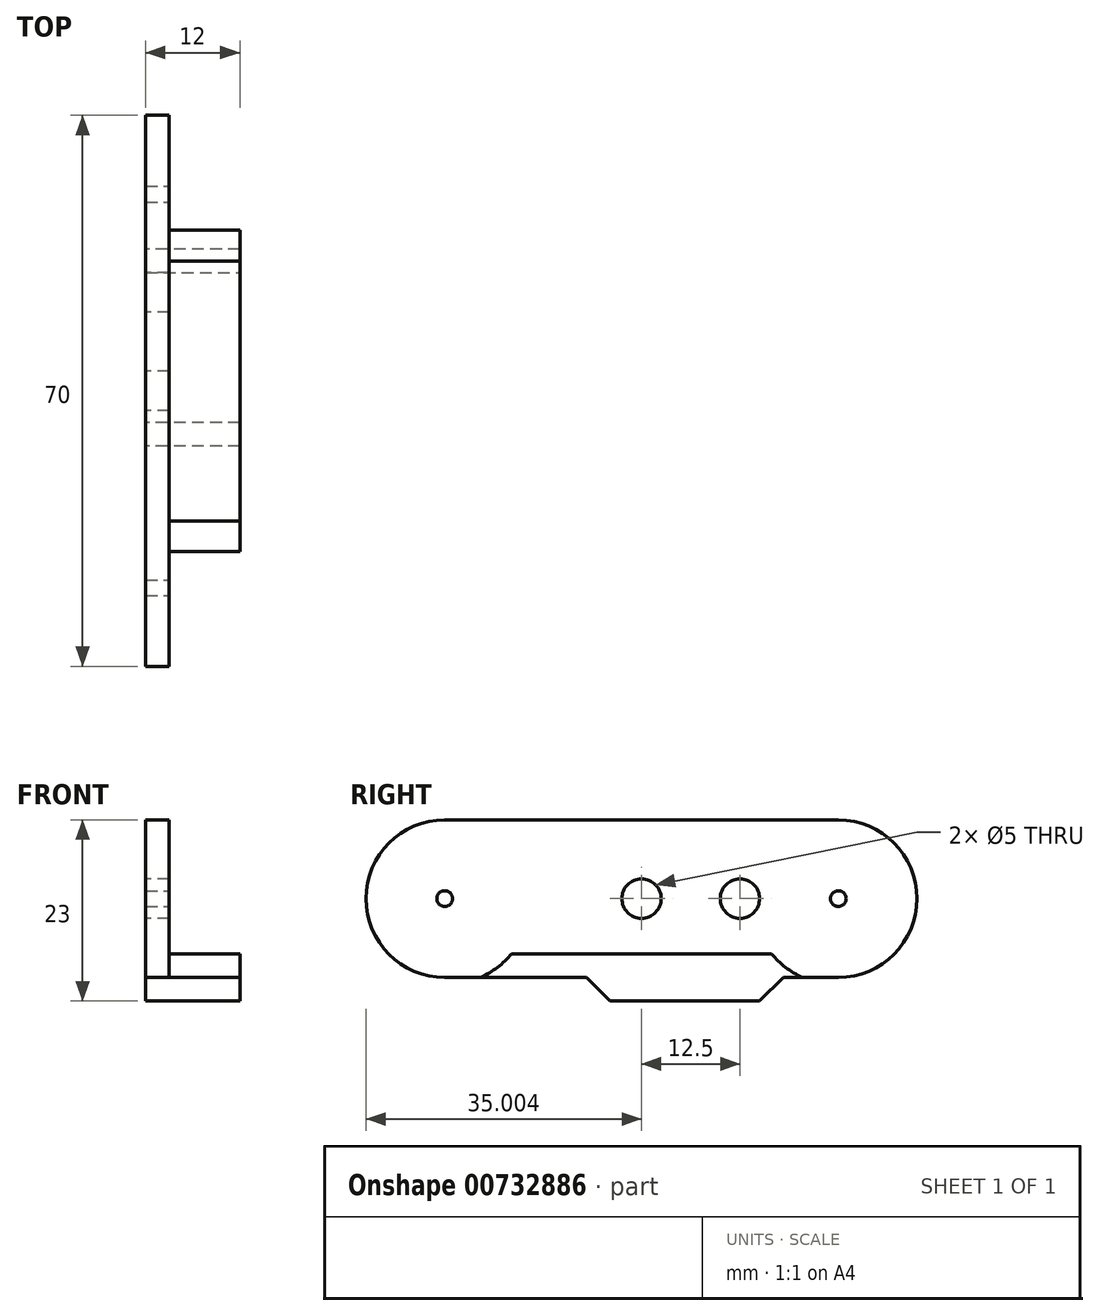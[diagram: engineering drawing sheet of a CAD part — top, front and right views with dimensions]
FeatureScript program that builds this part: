
annotation { "Feature Type Name" : "Feature", "Feature Type Description" : "" }
export const myFeature = defineFeature(function(context is Context, id is Id, definition is map)
    precondition{}
    {
        {
            var Q0;
            Q0=qCreatedBy(makeId("Right.planeOp"),FACE);
            var sketch = newSketch(context, id + "F0", { "sketchPlane" : qUnion([Q0])});
            skLineSegment(sketch, "E0.bottom", {"start": v(50.2, 39.59) * mm, "end": v(-19.8, 39.59) * mm});
            skLineSegment(sketch, "E0.top", {"start": v(50.2, 19.59) * mm, "end": v(-19.8, 19.59) * mm});
            skLineSegment(sketch, "E0.left", {"start": v(50.2, 39.59) * mm, "end": v(50.2, 19.59) * mm});
            skLineSegment(sketch, "E0.right", {"start": v(-19.8, 39.59) * mm, "end": v(-19.8, 19.59) * mm});
            skSolve(sketch);
        }
        {
            var Q0;
            Q0=makeQuery(id+"F0.imprint","IMPRINT",FACE,{"disambiguationData":[TD([[makeQuery(id+"F0.imprint","IMPRINT",EDGE,{"derivedFrom":sQuery(id+"F0.wireOp",EDGE,"E0.bottom")}),1.0]])]});
            extrude(context, id + "F1", {"entities" : qUnion([Q0]), "depth" : 3 * mm, "offsetDistance" : 25 * mm});
        }
        {
            var Q0;
            Q0=makeQuery(id+"F1.opExtrude","CAP_FACE",FACE,{"disambiguationData":[OSD([sQuery(id+"F0.wireOp",EDGE,"E0.bottom"),sQuery(id+"F0.wireOp",EDGE,"E0.top"),sQuery(id+"F0.wireOp",EDGE,"E0.left"),sQuery(id+"F0.wireOp",EDGE,"E0.right")])],"isStart":false});
            var sketch = newSketch(context, id + "F2", { "sketchPlane" : qUnion([Q0])});
            skLineSegment(sketch, "E1.bottom", {"start": v(-19.8, 19.59) * mm, "end": v(50.2, 19.59) * mm});
            skLineSegment(sketch, "E1.top", {"start": v(-19.8, 22.59) * mm, "end": v(50.2, 22.59) * mm});
            skLineSegment(sketch, "E1.left", {"start": v(-19.8, 19.59) * mm, "end": v(-19.8, 22.59) * mm});
            skLineSegment(sketch, "E1.right", {"start": v(50.2, 19.59) * mm, "end": v(50.2, 22.59) * mm});
            skLineSegment(sketch, "E2.bottom", {"start": v(-19.8, 39.59) * mm, "end": v(0.2, 39.59) * mm});
            skLineSegment(sketch, "E2.top", {"start": v(-19.8, 19.59) * mm, "end": v(0.2, 19.59) * mm});
            skLineSegment(sketch, "E2.left", {"start": v(-19.8, 39.59) * mm, "end": v(-19.8, 19.59) * mm});
            skLineSegment(sketch, "E2.right", {"start": v(0.2, 39.59) * mm, "end": v(0.2, 19.59) * mm});
            skLineSegment(sketch, "E3.bottom", {"start": v(50.2, 39.59) * mm, "end": v(40.2, 39.59) * mm});
            skLineSegment(sketch, "E3.top", {"start": v(50.2, 19.59) * mm, "end": v(40.2, 19.59) * mm});
            skLineSegment(sketch, "E3.left", {"start": v(50.2, 39.59) * mm, "end": v(50.2, 19.59) * mm});
            skLineSegment(sketch, "E3.right", {"start": v(40.2, 39.59) * mm, "end": v(40.2, 19.59) * mm});
            skCircle(sketch, "E4", {"center": v(40.2, 29.59) * mm, "radius": 11 * mm});
            skCircle(sketch, "E5", {"center": v(-9.8, 29.59) * mm, "radius": 11 * mm});
            skPoint(sketch, "E5.centerSnap0", {"position": v(-19.8, 29.59) * mm});
            skPoint(sketch, "E5.centerSnap1", {"position": v(-9.8, 39.59) * mm});
            skSolve(sketch);
        }
        {
            var Q0;
            {var subQ0=sQuery(id+"F2.wireOp",EDGE,"E5");var subQ1=sQuery(id+"F2.wireOp",EDGE,"E1.top");var subQ2=makeQuery(id+"F2.imprint","INTERSECT",VERTEX,{"disambiguationData":[OD(1.0)],"derivedFrom":[subQ1,subQ0]});Q0=makeQuery(id+"F2.imprint","IMPRINT",FACE,{"disambiguationData":[TD([[makeQuery(id+"F2.imprint","IMPRINT",EDGE,{"disambiguationData":[TD([[subQ2,-1.0]])],"derivedFrom":subQ1}),-1.0]])]});}
            var Q1;
            {var subQ0=sQuery(id+"F2.wireOp",EDGE,"E2.right");var subQ5=sQuery(id+"F2.wireOp",EDGE,"E1.top");var subQ7=makeQuery(id+"F2.imprint","INTERSECT",VERTEX,{"derivedFrom":[subQ5,subQ0]});Q1=makeQuery(id+"F2.imprint","IMPRINT",FACE,{"disambiguationData":[TD([[makeQuery(id+"F2.imprint","IMPRINT",EDGE,{"disambiguationData":[TD([[subQ7,-1.0]])],"derivedFrom":subQ5}),-1.0]])]});}
            extrude(context, id + "F3", {"entities" : qUnion([Q0, Q1]), "operationType" : NewBodyOperationType.ADD, "depth" : 9 * mm, "offsetDistance" : 25 * mm});
        }
        {
            var Q0;
            Q0=makeQuery(id+"F1.opExtrude","CAP_FACE",FACE,{"disambiguationData":[OSD([sQuery(id+"F0.wireOp",EDGE,"E0.bottom"),sQuery(id+"F0.wireOp",EDGE,"E0.top"),sQuery(id+"F0.wireOp",EDGE,"E0.left"),sQuery(id+"F0.wireOp",EDGE,"E0.right")])],"isStart":true});
            var sketch = newSketch(context, id + "F4", { "sketchPlane" : qUnion([Q0])});
            skLineSegment(sketch, "E6.bottom", {"start": v(19.8, 39.59) * mm, "end": v(-0.2, 39.59) * mm});
            skLineSegment(sketch, "E6.top", {"start": v(19.8, 19.59) * mm, "end": v(-0.2, 19.59) * mm});
            skLineSegment(sketch, "E6.left", {"start": v(19.8, 39.59) * mm, "end": v(19.8, 19.59) * mm});
            skLineSegment(sketch, "E6.right", {"start": v(-0.2, 39.59) * mm, "end": v(-0.2, 19.59) * mm});
            skCircle(sketch, "E7", {"center": v(9.8, 29.59) * mm, "radius": 10 * mm});
            skLineSegment(sketch, "E8.bottom", {"start": v(9.8, 29.59) * mm, "end": v(-20.2, 29.59) * mm});
            skLineSegment(sketch, "E8.top", {"start": v(9.8, -0.41) * mm, "end": v(-20.2, -0.41) * mm});
            skLineSegment(sketch, "E8.left", {"start": v(9.8, 29.59) * mm, "end": v(9.8, -0.41) * mm});
            skLineSegment(sketch, "E8.right", {"start": v(-20.2, 29.59) * mm, "end": v(-20.2, -0.41) * mm});
            skLineSegment(sketch, "E9", {"start": v(9.8, 29.59) * mm, "end": v(-20.2, -0.41) * mm});
            skLineSegment(sketch, "E10", {"start": v(9.8, 29.59) * mm, "end": v(-4.35, 15.45) * mm});
            skCircle(sketch, "E11", {"center": v(-4.35, 15.45) * mm, "radius": 10 * mm});
            skCircle(sketch, "E12", {"center": v(-20.2, -0.41) * mm, "radius": 10 * mm});
            skLineSegment(sketch, "E13.bottom", {"start": v(-14.35, 25.45) * mm, "end": v(5.65, 25.45) * mm});
            skLineSegment(sketch, "E13.top", {"start": v(-14.35, 5.45) * mm, "end": v(5.65, 5.45) * mm});
            skLineSegment(sketch, "E13.left", {"start": v(-14.35, 25.45) * mm, "end": v(-14.35, 5.45) * mm});
            skLineSegment(sketch, "E13.right", {"start": v(5.65, 25.45) * mm, "end": v(5.65, 5.45) * mm});
            skLineSegment(sketch, "E14", {"start": v(-14.35, 25.45) * mm, "end": v(5.65, 5.45) * mm});
            skLineSegment(sketch, "E15.bottom", {"start": v(-30.2, 9.59) * mm, "end": v(-10.2, 9.59) * mm});
            skLineSegment(sketch, "E15.top", {"start": v(-30.2, -10.41) * mm, "end": v(-10.2, -10.41) * mm});
            skLineSegment(sketch, "E15.left", {"start": v(-30.2, 9.59) * mm, "end": v(-30.2, -10.41) * mm});
            skLineSegment(sketch, "E15.right", {"start": v(-10.2, 9.59) * mm, "end": v(-10.2, -10.41) * mm});
            skLineSegment(sketch, "E16", {"start": v(-30.2, 9.59) * mm, "end": v(-10.2, -10.41) * mm});
            skLineSegment(sketch, "E17", {"start": v(-11.42, 22.52) * mm, "end": v(-27.28, 6.66) * mm});
            skLineSegment(sketch, "E18.bottom", {"start": v(-50.2, 39.59) * mm, "end": v(-30.2, 39.59) * mm});
            skLineSegment(sketch, "E18.top", {"start": v(-50.2, 19.59) * mm, "end": v(-30.2, 19.59) * mm});
            skLineSegment(sketch, "E18.left", {"start": v(-50.2, 39.59) * mm, "end": v(-50.2, 19.59) * mm});
            skLineSegment(sketch, "E18.right", {"start": v(-30.2, 39.59) * mm, "end": v(-30.2, 19.59) * mm});
            skCircle(sketch, "E19", {"center": v(-40.2, 29.59) * mm, "radius": 10 * mm});
            skLineSegment(sketch, "E20", {"start": v(9.8, 19.59) * mm, "end": v(0, 24.45) * mm});
            skSolve(sketch);
        }
        {
            var Q0;
            {var subQ0=sQuery(id+"F4.wireOp",EDGE,"E6.left");var subQ1=sQuery(id+"F4.wireOp",EDGE,"E6.bottom");var subQ2=makeQuery(id+"F4.imprint","INTERSECT",VERTEX,{"derivedFrom":[subQ1,subQ0]});Q0=makeQuery(id+"F4.imprint","IMPRINT",FACE,{"disambiguationData":[TD([[makeQuery(id+"F4.imprint","IMPRINT",EDGE,{"disambiguationData":[TD([[subQ2,1.0]])],"derivedFrom":subQ1}),-1.0]])]});}
            var Q1;
            {var subQ0=sQuery(id+"F4.wireOp",EDGE,"E6.left");var subQ1=sQuery(id+"F4.wireOp",EDGE,"E6.top");var subQ2=makeQuery(id+"F4.imprint","INTERSECT",VERTEX,{"derivedFrom":[subQ1,subQ0]});Q1=makeQuery(id+"F4.imprint","IMPRINT",FACE,{"disambiguationData":[TD([[makeQuery(id+"F4.imprint","IMPRINT",EDGE,{"disambiguationData":[TD([[subQ2,1.0]])],"derivedFrom":subQ0}),-1.0]])]});}
            var Q2;
            {var subQ0=sQuery(id+"F4.wireOp",EDGE,"E18.left");var subQ1=sQuery(id+"F4.wireOp",EDGE,"E18.bottom");var subQ2=makeQuery(id+"F4.imprint","INTERSECT",VERTEX,{"derivedFrom":[subQ1,subQ0]});Q2=makeQuery(id+"F4.imprint","IMPRINT",FACE,{"disambiguationData":[TD([[makeQuery(id+"F4.imprint","IMPRINT",EDGE,{"disambiguationData":[TD([[subQ2,-1.0]])],"derivedFrom":subQ1}),-1.0]])]});}
            var Q3;
            {var subQ0=sQuery(id+"F4.wireOp",EDGE,"E18.left");var subQ1=sQuery(id+"F4.wireOp",EDGE,"E18.top");var subQ2=makeQuery(id+"F4.imprint","INTERSECT",VERTEX,{"derivedFrom":[subQ1,subQ0]});Q3=makeQuery(id+"F4.imprint","IMPRINT",FACE,{"disambiguationData":[TD([[makeQuery(id+"F4.imprint","IMPRINT",EDGE,{"disambiguationData":[TD([[subQ2,-1.0]])],"derivedFrom":subQ1}),1.0]])]});}
            extrude(context, id + "F5", {"entities" : qUnion([Q0, Q1, Q2, Q3]), "operationType" : NewBodyOperationType.REMOVE, "oppositeDirection" : true, "depth" : 25 * mm, "offsetDistance" : 25 * mm});
        }
        {
            var Q0;
            Q0=makeQuery(id+"F1.opExtrude","CAP_FACE",FACE,{"disambiguationData":[OSD([sQuery(id+"F0.wireOp",EDGE,"E0.bottom"),sQuery(id+"F0.wireOp",EDGE,"E0.top"),sQuery(id+"F0.wireOp",EDGE,"E0.left"),sQuery(id+"F0.wireOp",EDGE,"E0.right")])],"isStart":false});
            var sketch = newSketch(context, id + "F6", { "sketchPlane" : qUnion([Q0])});
            skCircle(sketch, "E21", {"center": v(-9.8, 29.59) * mm, "radius": 1 * mm});
            skCircle(sketch, "E22", {"center": v(40.2, 29.59) * mm, "radius": 1 * mm});
            skSolve(sketch);
        }
        {
            var Q0;
            Q0=makeQuery(id+"F6.imprint","IMPRINT",FACE,{"disambiguationData":[TD([[makeQuery(id+"F6.imprint","IMPRINT",EDGE,{"derivedFrom":sQuery(id+"F6.wireOp",EDGE,"E21")}),1.0]])]});
            var Q1;
            Q1=makeQuery(id+"F6.imprint","IMPRINT",FACE,{"disambiguationData":[TD([[makeQuery(id+"F6.imprint","IMPRINT",EDGE,{"derivedFrom":sQuery(id+"F6.wireOp",EDGE,"E22")}),1.0]])]});
            extrude(context, id + "F7", {"entities" : qUnion([Q0, Q1]), "operationType" : NewBodyOperationType.REMOVE, "oppositeDirection" : true, "depth" : 25 * mm, "offsetDistance" : 25 * mm});
        }
        {
            var Q0;
            Q0=makeQuery(id+"F1.opExtrude","CAP_FACE",FACE,{"disambiguationData":[OSD([sQuery(id+"F0.wireOp",EDGE,"E0.bottom"),sQuery(id+"F0.wireOp",EDGE,"E0.top"),sQuery(id+"F0.wireOp",EDGE,"E0.left"),sQuery(id+"F0.wireOp",EDGE,"E0.right")])],"isStart":true});
            var sketch = newSketch(context, id + "F8", { "sketchPlane" : qUnion([Q0])});
            skCircle(sketch, "E23", {"center": v(-40.2, 29.59) * mm, "radius": 2.71 * mm});
            skCircle(sketch, "E24", {"center": v(-15.2, 29.59) * mm, "radius": 2.5 * mm});
            skPoint(sketch, "E24.centerSnap0", {"position": v(-15.2, 39.59) * mm});
            skCircle(sketch, "E25", {"center": v(-27.7, 29.59) * mm, "radius": 2.5 * mm});
            skSolve(sketch);
        }
        {
            var Q0;
            Q0=makeQuery(id+"F8.imprint","IMPRINT",FACE,{"disambiguationData":[TD([[makeQuery(id+"F8.imprint","IMPRINT",EDGE,{"derivedFrom":sQuery(id+"F8.wireOp",EDGE,"E25")}),1.0]])]});
            var Q1;
            Q1=makeQuery(id+"F8.imprint","IMPRINT",FACE,{"disambiguationData":[TD([[makeQuery(id+"F8.imprint","IMPRINT",EDGE,{"derivedFrom":sQuery(id+"F8.wireOp",EDGE,"E24")}),1.0]])]});
            extrude(context, id + "F9", {"entities" : qUnion([Q0, Q1]), "operationType" : NewBodyOperationType.REMOVE, "oppositeDirection" : true, "depth" : 25 * mm, "offsetDistance" : 25 * mm});
        }
        {
            var Q0;
            Q0=makeQuery(id+"F1.opExtrude","CAP_FACE",FACE,{"disambiguationData":[OSD([sQuery(id+"F0.wireOp",EDGE,"E0.bottom"),sQuery(id+"F0.wireOp",EDGE,"E0.top"),sQuery(id+"F0.wireOp",EDGE,"E0.left"),sQuery(id+"F0.wireOp",EDGE,"E0.right")])],"isStart":true});
            var sketch = newSketch(context, id + "F10", { "sketchPlane" : qUnion([Q0])});
            skLineSegment(sketch, "E26.bottom", {"start": v(-8.2, 19.59) * mm, "end": v(-33.2, 19.59) * mm});
            skLineSegment(sketch, "E26.top", {"start": v(-8.2, 16.59) * mm, "end": v(-33.2, 16.59) * mm});
            skLineSegment(sketch, "E26.left", {"start": v(-8.2, 19.59) * mm, "end": v(-8.2, 16.59) * mm});
            skLineSegment(sketch, "E26.right", {"start": v(-33.2, 19.59) * mm, "end": v(-33.2, 16.59) * mm});
            skCircle(sketch, "E27", {"center": v(9.8, 29.59) * mm, "radius": 2.5 * mm});
            skLineSegment(sketch, "E28.bottom", {"start": v(-15.2, 16.59) * mm, "end": v(-12.2, 16.59) * mm});
            skLineSegment(sketch, "E28.top", {"start": v(-15.2, 13.59) * mm, "end": v(-12.2, 13.59) * mm});
            skLineSegment(sketch, "E28.left", {"start": v(-15.2, 16.59) * mm, "end": v(-15.2, 13.59) * mm});
            skLineSegment(sketch, "E28.right", {"start": v(-12.2, 16.59) * mm, "end": v(-12.2, 13.59) * mm});
            skCircle(sketch, "E29", {"center": v(-40.2, 29.59) * mm, "radius": 2.42 * mm});
            skSolve(sketch);
        }
        {
            var Q0;
            Q0=makeQuery(id+"F10.imprint","IMPRINT",FACE,{"disambiguationData":[TD([[makeQuery(id+"F10.imprint","IMPRINT",EDGE,{"derivedFrom":sQuery(id+"F10.wireOp",EDGE,"E26.bottom")}),-1.0]])]});
            var Q1;
            Q1=makeQuery(id+"F10.imprint","IMPRINT",FACE,{"disambiguationData":[TD([[makeQuery(id+"F10.imprint","IMPRINT",EDGE,{"derivedFrom":sQuery(id+"F10.wireOp",EDGE,"E28.bottom")}),-1.0]])]});
            extrude(context, id + "F11", {"entities" : qUnion([Q0, Q1]), "operationType" : NewBodyOperationType.ADD, "depth" : -12 * mm, "offsetDistance" : 25 * mm});
        }
        {
            var Q0;
            Q0=makeQuery(id+"F11.opExtrude","SWEPT_EDGE",EDGE,{"disambiguationData":[OSD([sQuery(id+"F10.wireOp",EDGE,"E26.top"),sQuery(id+"F10.wireOp",EDGE,"E26.left")])]});
            var Q1;
            Q1=makeQuery(id+"F11.opExtrude","SWEPT_EDGE",EDGE,{"disambiguationData":[OSD([sQuery(id+"F10.wireOp",EDGE,"E26.top"),sQuery(id+"F10.wireOp",EDGE,"E26.right")])]});
            chamfer(context, id + "F12", {"entities" : qUnion([Q0, Q1]), "width" : 3 * mm, "tangentPropagation" : true});
        }
    });
